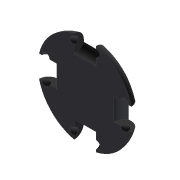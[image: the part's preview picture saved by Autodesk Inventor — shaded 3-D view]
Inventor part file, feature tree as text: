
AUTODESK INVENTOR PART (.ipt)
format: ipt  version: 2017 (Build 210142000, 142)  size: 146,944 bytes
history: native  units: mm
features: sketch x2, extrude x1, fillet x1, revolve x1, pattern_circular x1
ambient origin geometry x8: Origin, YZ Plane, XZ Plane, XY Plane, X Axis, Y Axis, Z Axis, Center Point
bodies: Solid1 (feature_tree)
feature tree (6):
  extrude  "Extrusion1"  Depth=6.0mm TaperAngle=0.0deg
  fillet  "Fillet1"  Radius=6.0mm
  revolve  "Revolution1"  [1 undecoded]
  pattern_circular  "Circular Pattern1"  [2 undecoded]
  sketch  "Sketch1"  dims[d0=60.0mm d1=6.0mm d2=0.0mm d3=6.0mm]
  sketch  "Sketch2"  dims[d4=14.0mm d5=7.0mm d6=18.0mm d7=5.0mm d8=5.0mm d9=90.0deg d10=40.0mm d11=360.0deg]
note: 3 required parameter values undecoded (feature->parameter linkage not recoverable at this tier; creation-order binding heuristic only, values carry confidence <= 0.55)